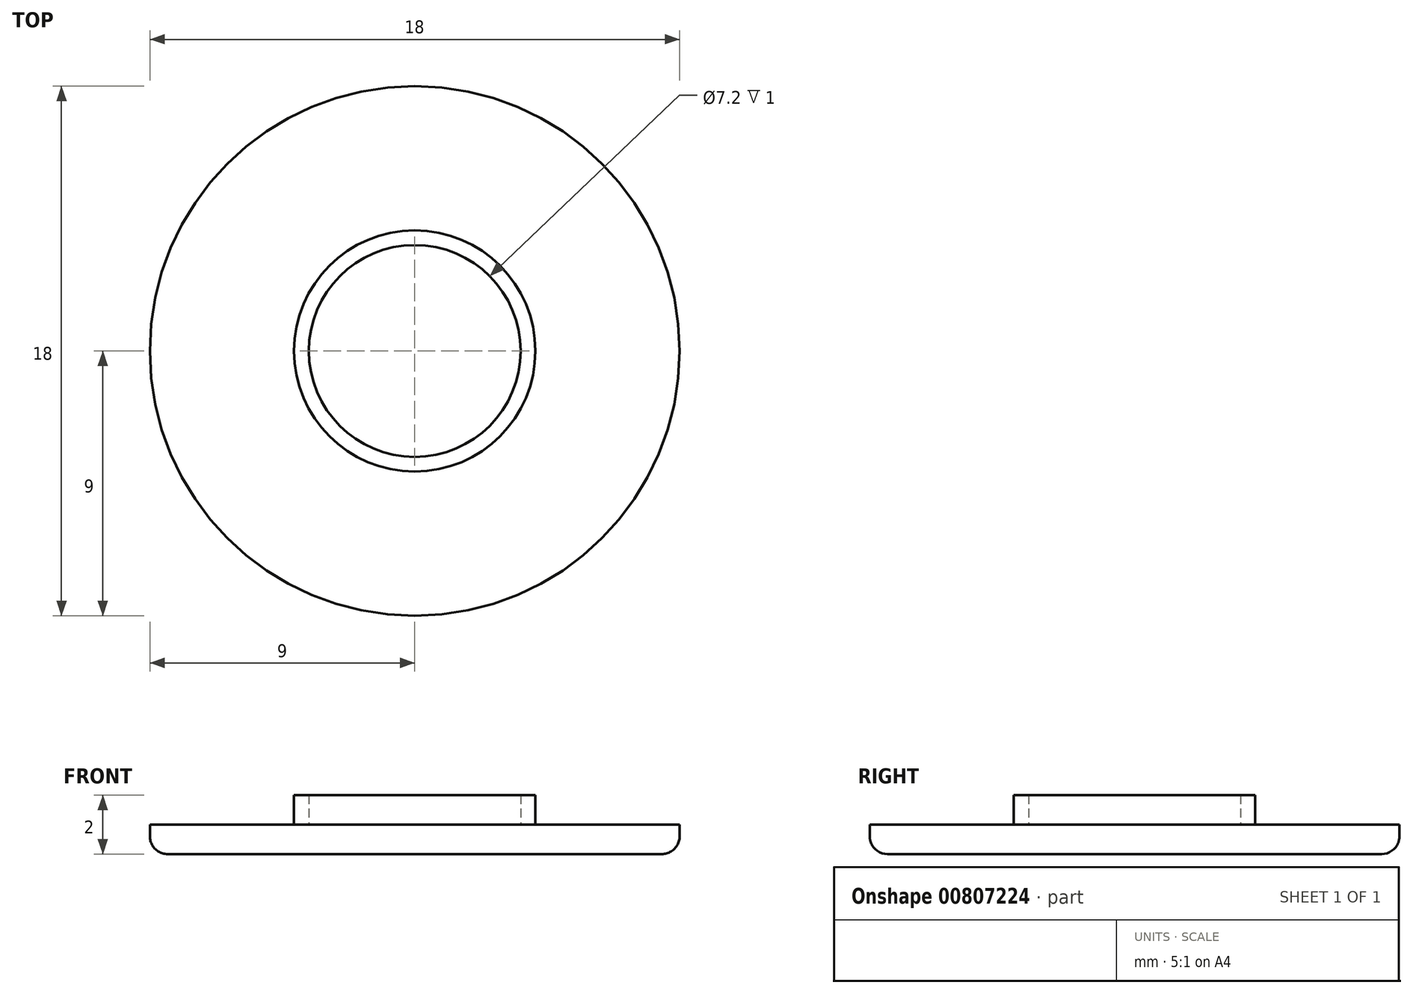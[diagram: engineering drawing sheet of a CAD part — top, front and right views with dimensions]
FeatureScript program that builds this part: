
annotation { "Feature Type Name" : "Feature", "Feature Type Description" : "" }
export const myFeature = defineFeature(function(context is Context, id is Id, definition is map)
    precondition{}
    {
        {
            var Q0;
            Q0=qCreatedBy(makeId("Top.planeOp"),FACE);
            var sketch = newSketch(context, id + "F0", { "sketchPlane" : qUnion([Q0])});
            skCircle(sketch, "E0", {"center": v(0, 0) * mm, "radius": 9 * mm});
            skCircle(sketch, "E1", {"center": v(0, 0) * mm, "radius": 3.6 * mm});
            skCircle(sketch, "E2", {"center": v(0, 0) * mm, "radius": 4.1 * mm});
            skSolve(sketch);
        }
        {
            var Q0;
            Q0=makeQuery(id+"F0.imprint","IMPRINT",FACE,{"disambiguationData":[TD([[makeQuery(id+"F0.imprint","IMPRINT",EDGE,{"derivedFrom":sQuery(id+"F0.wireOp",EDGE,"E0")}),1.0]])]});
            var Q1;
            Q1=makeQuery(id+"F0.imprint","IMPRINT",FACE,{"disambiguationData":[TD([[makeQuery(id+"F0.imprint","IMPRINT",EDGE,{"derivedFrom":sQuery(id+"F0.wireOp",EDGE,"E1")}),1.0]])]});
            extrude(context, id + "F1", {"entities" : qUnion([Q0, Q1]), "depth" : 1 * mm, "offsetDistance" : 25 * mm});
        }
        {
            var Q0;
            Q0=makeQuery(id+"F0.imprint","IMPRINT",FACE,{"disambiguationData":[TD([[makeQuery(id+"F0.imprint","IMPRINT",EDGE,{"derivedFrom":sQuery(id+"F0.wireOp",EDGE,"E1")}),-1.0]])]});
            extrude(context, id + "F2", {"entities" : qUnion([Q0]), "operationType" : NewBodyOperationType.ADD, "depth" : 2 * mm, "offsetDistance" : 25 * mm});
        }
        {
            var Q0;
            Q0=makeQuery(id+"F1.opExtrude","CAP_EDGE",EDGE,{"disambiguationData":[OSD([sQuery(id+"F0.wireOp",EDGE,"E0")])],"isStart":true});
            fillet(context, id + "F3", {"entities" : qUnion([Q0]), "radius" : 0.6 * mm, "tangentPropagation" : true, "allowEdgeOverflow" : false});
        }
    });
